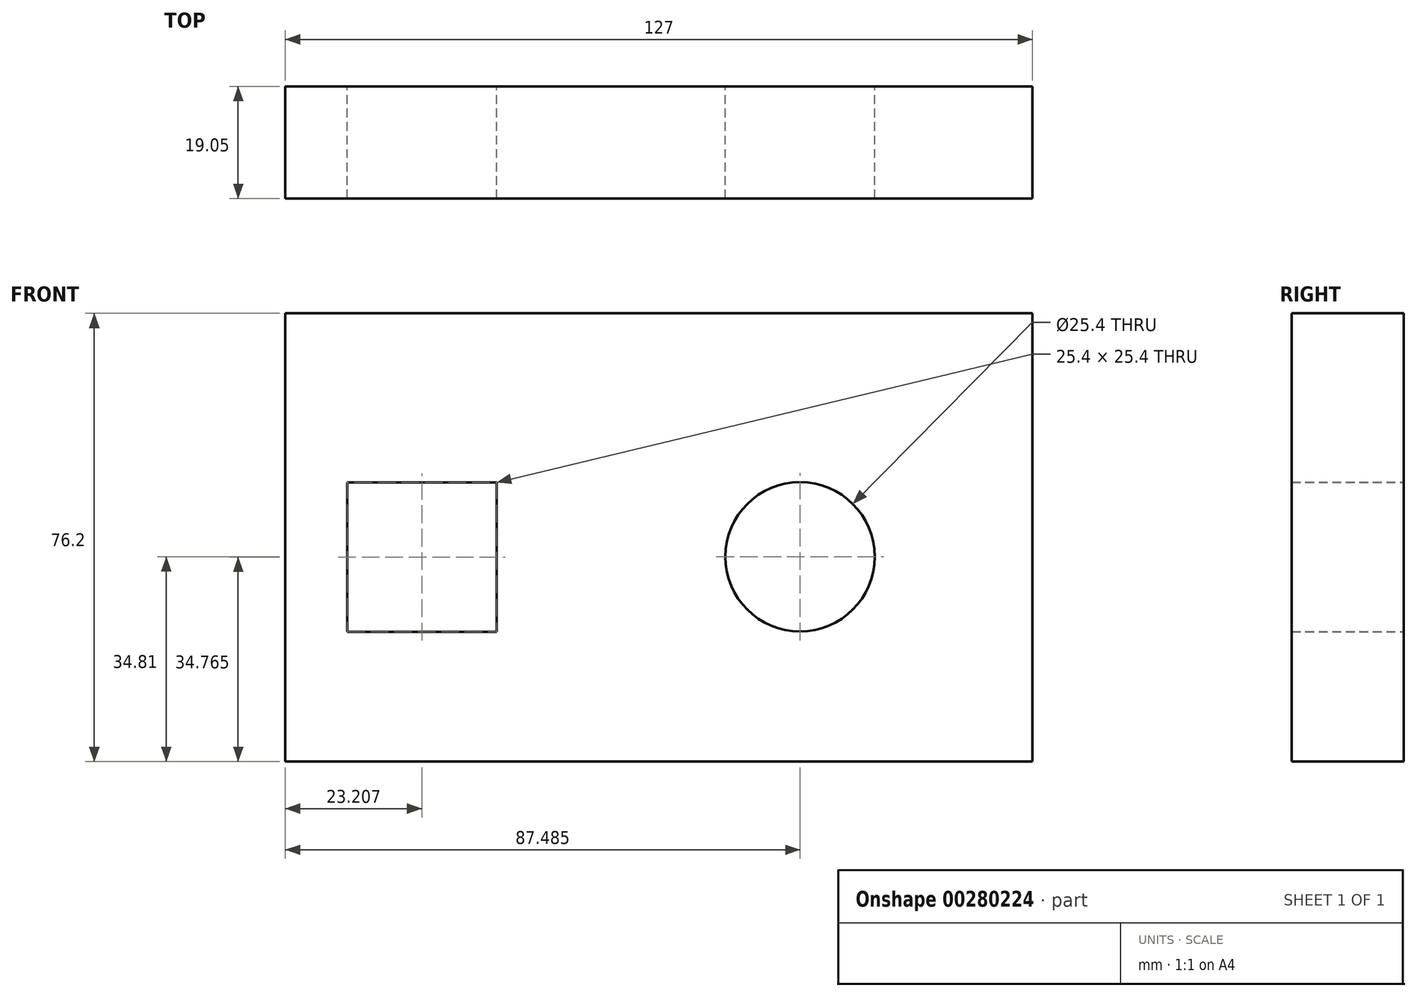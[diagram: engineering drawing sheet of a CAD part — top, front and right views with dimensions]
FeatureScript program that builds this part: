
annotation { "Feature Type Name" : "Feature", "Feature Type Description" : "" }
export const myFeature = defineFeature(function(context is Context, id is Id, definition is map)
    precondition{}
    {
        {
            var Q0;
            Q0=qCreatedBy(makeId("Front.planeOp"),FACE);
            var sketch = newSketch(context, id + "F0", { "sketchPlane" : qUnion([Q0])});
            skLineSegment(sketch, "E0", {"start": v(0, 0) * mm, "end": v(0, 76.2) * mm});
            skLineSegment(sketch, "E1", {"start": v(0, 76.2) * mm, "end": v(-127, 76.2) * mm});
            skLineSegment(sketch, "E2", {"start": v(-127, 76.2) * mm, "end": v(-127, 0) * mm});
            skLineSegment(sketch, "E3", {"start": v(-127, 0) * mm, "end": v(0, 0) * mm});
            skCircle(sketch, "E4", {"center": v(-39.51, 34.81) * mm, "radius": 12.7 * mm});
            skLineSegment(sketch, "E5.bottom", {"start": v(-91.1, 22.07) * mm, "end": v(-116.5, 22.07) * mm});
            skLineSegment(sketch, "E5.top", {"start": v(-91.1, 47.47) * mm, "end": v(-116.5, 47.47) * mm});
            skLineSegment(sketch, "E5.left", {"start": v(-91.1, 22.07) * mm, "end": v(-91.1, 47.47) * mm});
            skLineSegment(sketch, "E5.right", {"start": v(-116.5, 22.07) * mm, "end": v(-116.5, 47.47) * mm});
            skSolve(sketch);
        }
        {
            var Q0;
            Q0 = qSketchRegion(id + "F0", true);
            extrude(context, id + "F1", {"entities" : qUnion([Q0]), "depth" : 19.05 * mm});
        }
    });
